FCSTD DOCUMENT  (FreeCAD 1.0R39319 (Git))
Label: Terminal_Front_View
License: All rights reserved
LicenseURL: https://en.wikipedia.org/wiki/All_rights_reserved
objects: Sketcher::SketchObject×1
note: 2 computed .brp shape members not serialized (recipe doc carries the construction recipe); baked Part::Feature solids carry a one-line shape summary decoded from their .brp

FEATURE [Sketcher::SketchObject] Sketch
  ArcFitTolerance = 1e-06
  FullyConstrained = true
  MakeInternals = false
  sketch-geometry (8):
    g0: Circle CenterX=9.5 CenterY=0 CenterZ=0 NormalX=0 NormalY=0 NormalZ=1 AngleXU=0 Radius=5
    g1: Circle CenterX=-9.5 CenterY=0 CenterZ=0 NormalX=0 NormalY=0 NormalZ=1 AngleXU=0 Radius=5
    g2: Circle CenterX=28.3944 CenterY=-2 CenterZ=0 NormalX=0 NormalY=0 NormalZ=1 AngleXU=0 Radius=5
    g3: Circle CenterX=-28.3944 CenterY=-2 CenterZ=0 NormalX=0 NormalY=0 NormalZ=1 AngleXU=0 Radius=5
    g4: Circle CenterX=-28.3944 CenterY=-2 CenterZ=0 NormalX=0 NormalY=0 NormalZ=1 AngleXU=0 Radius=2
    g5: Circle CenterX=-9.5 CenterY=0 CenterZ=0 NormalX=0 NormalY=0 NormalZ=1 AngleXU=0 Radius=2
    g6: Circle CenterX=9.5 CenterY=0 CenterZ=0 NormalX=0 NormalY=0 NormalZ=1 AngleXU=0 Radius=2
    g7: Circle CenterX=28.3944 CenterY=-2 CenterZ=0 NormalX=0 NormalY=0 NormalZ=1 AngleXU=0 Radius=2
  constraints (18):
    c: Symmetric(g1,g0,g-2)
    c: Symmetric(g2,g3,g-2)
    c: Equal(g1,g0)
    c: Equal(g1,g2)
    c: Equal(g1,g3)
    c: Diameter(g1) = 10
    c: Distance(g1,g0) = 19
    c: Distance(g0,g2) = 19
    c: PointOnObject(g0,g-1)
    c: DistanceY(g2,g-1) = 2
    c: Coincident(g4,g3)
    c: Coincident(g5,g1)
    c: Coincident(g6,g0)
    c: Coincident(g7,g2)
    c: Equal(g7,g6)
    c: Equal(g7,g5)
    c: Equal(g7,g4)
    c: Diameter(g7) = 4
